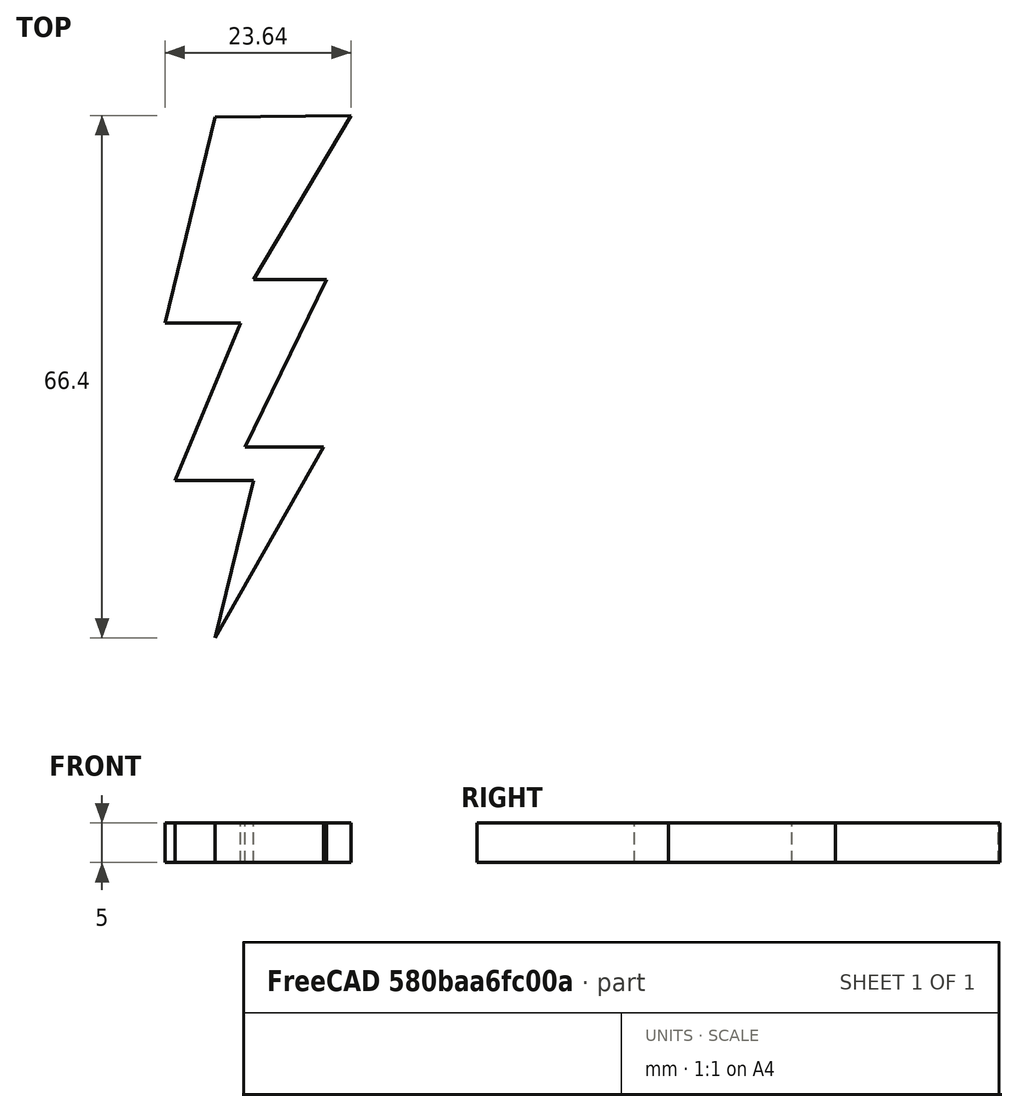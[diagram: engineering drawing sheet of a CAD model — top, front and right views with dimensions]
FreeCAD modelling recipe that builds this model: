
FCSTD DOCUMENT  (FreeCAD 0.16R6707 (Git))
Label: Rayo
License: CreativeCommons Attribution-ShareAlike
LicenseURL: http://creativecommons.org/licenses/by-sa/4.0/
objects: Sketcher::SketchObject×1, PartDesign::Pad×1
note: 3 computed .brp shape members not serialized (recipe doc carries the construction recipe); baked Part::Feature solids carry a one-line shape summary decoded from their .brp

FEATURE [Sketcher::SketchObject] Sketch  label="Boceto_rayo"
  sketch-geometry (11):
    g0: LineSegment StartX=0 StartY=0 StartZ=0 EndX=4.89483 EndY=20 EndZ=0
    g1: LineSegment StartX=4.89483 StartY=20 StartZ=0 EndX=-5.07954 EndY=20 EndZ=0
    g2: LineSegment StartX=-5.07954 StartY=20 StartZ=0 EndX=3.23243 EndY=40 EndZ=0
    g3: LineSegment StartX=3.23243 StartY=40 StartZ=0 EndX=-6.37251 EndY=40 EndZ=0
    g4: LineSegment StartX=-6.37251 StartY=40 StartZ=0 EndX=0 EndY=66.2187 EndZ=0
    g5: LineSegment StartX=0 StartY=66.2187 StartZ=0 EndX=17.2704 EndY=66.4034 EndZ=0
    g6: LineSegment StartX=17.2704 StartY=66.4034 StartZ=0 EndX=4.89483 EndY=45.5311 EndZ=0
    g7: LineSegment StartX=4.89483 StartY=45.5311 StartZ=0 EndX=14.1304 EndY=45.5311 EndZ=0
    g8: LineSegment StartX=14.1304 StartY=45.5311 StartZ=0 EndX=3.78656 EndY=24.2894 EndZ=0
    g9: LineSegment StartX=3.78656 StartY=24.2894 StartZ=0 EndX=13.7609 EndY=24.2894 EndZ=0
    g10: LineSegment StartX=13.7609 StartY=24.2894 StartZ=0 EndX=0 EndY=0 EndZ=0
  constraints (10):
    c: Coincident(g0,g1)
    c: Coincident(g1,g2)
    c: Coincident(g2,g3)
    c: Coincident(g3,g4)
    c: Coincident(g4,g5)
    c: Coincident(g5,g6)
    c: Coincident(g6,g7)
    c: Coincident(g7,g8)
    c: Coincident(g8,g9)
    c: Coincident(g9,g10)
FEATURE [PartDesign::Pad] Pad  label="Rayo"
  Length = 5
  Length2 = 100
  Sketch = -> Sketch
  Type = 0
